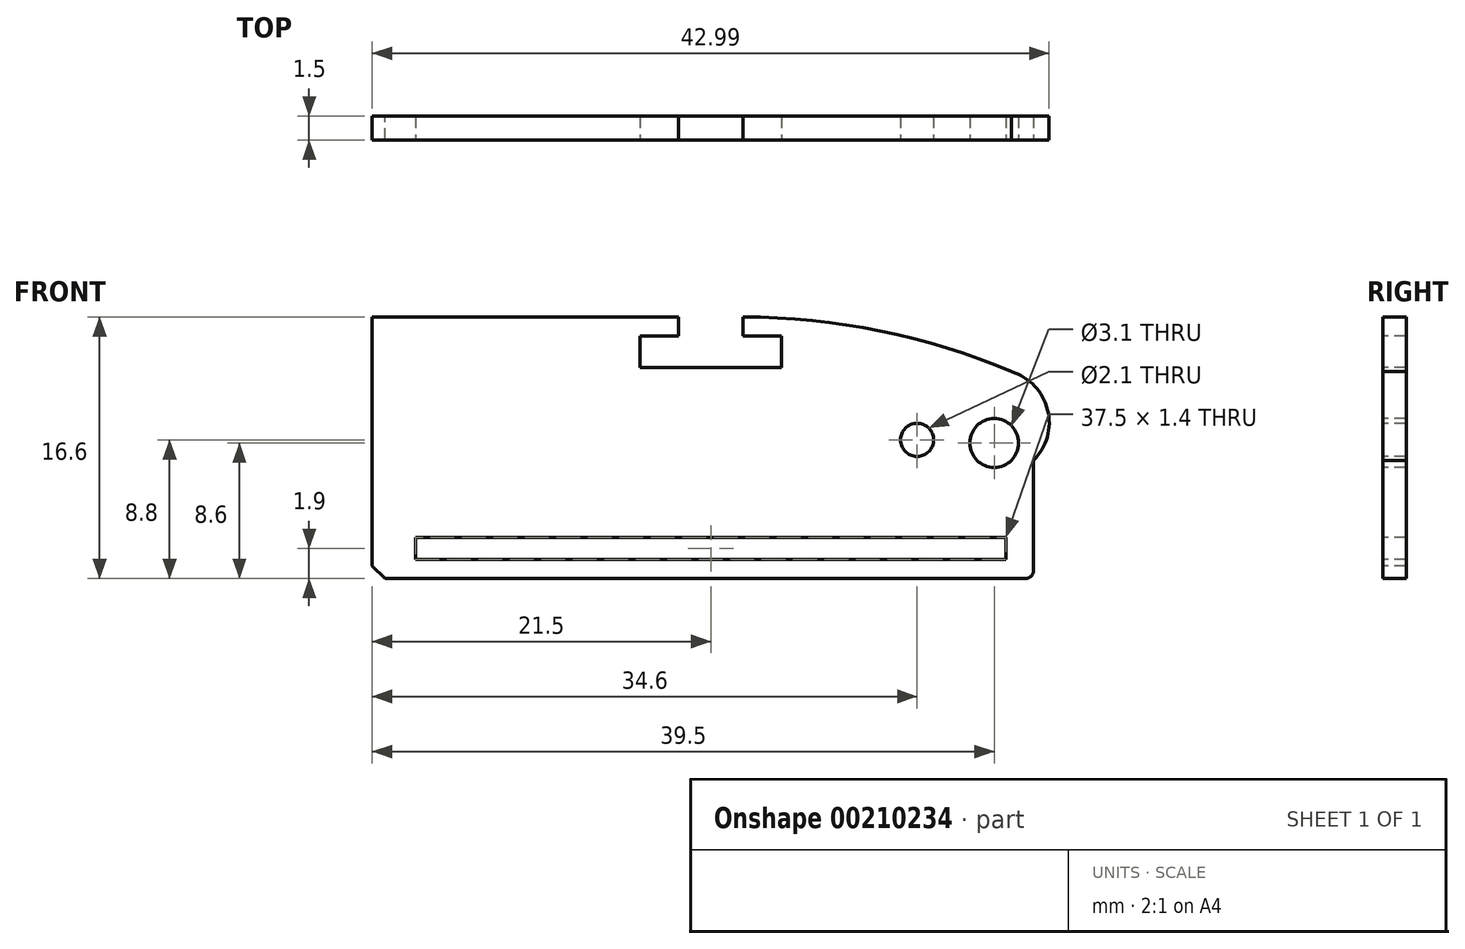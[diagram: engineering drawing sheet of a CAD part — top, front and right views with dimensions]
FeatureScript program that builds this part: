
annotation { "Feature Type Name" : "Feature", "Feature Type Description" : "" }
export const myFeature = defineFeature(function(context is Context, id is Id, definition is map)
    precondition{}
    {
        {
            var Q0;
            Q0=qCreatedBy(makeId("Front.planeOp"),FACE);
            var sketch = newSketch(context, id + "F0", { "sketchPlane" : qUnion([Q0])});
            skLineSegment(sketch, "E0.bottom", {"start": v(-21.5, 8.3) * mm, "end": v(21.5, 8.3) * mm});
            skLineSegment(sketch, "E0.top", {"start": v(-21.5, -8.3) * mm, "end": v(21.5, -8.3) * mm});
            skLineSegment(sketch, "E0.left", {"start": v(-21.5, 8.3) * mm, "end": v(-21.5, -8.3) * mm});
            skLineSegment(sketch, "E0.right", {"start": v(21.5, 8.3) * mm, "end": v(21.5, -8.3) * mm});
            skPoint(sketch, "E0.middle", {"position": v(0, 0) * mm});
            skPoint(sketch, "E1.middle", {"position": v(0, -8.3) * mm});
            skPoint(sketch, "E2.middle", {"position": v(0, -1.7) * mm});
            skSolve(sketch);
        }
        {
            var Q0;
            Q0=makeQuery(id+"F0.imprint","IMPRINT",FACE,{"disambiguationData":[TD([[makeQuery(id+"F0.imprint","IMPRINT",EDGE,{"derivedFrom":sQuery(id+"F0.wireOp",EDGE,"E0.bottom")}),-1.0]])]});
            extrude(context, id + "F1", {"entities" : qUnion([Q0]), "endBound" : BoundingType.SYMMETRIC, "depth" : 1.5 * mm});
        }
        {
            var Q0;
            Q0=qCreatedBy(makeId("Front.planeOp"),FACE);
            var sketch = newSketch(context, id + "F2", { "sketchPlane" : qUnion([Q0])});
            skLineSegment(sketch, "E3.bottom", {"start": v(-18.75, -5.7) * mm, "end": v(18.75, -5.7) * mm});
            skLineSegment(sketch, "E3.top", {"start": v(-18.75, -7.1) * mm, "end": v(18.75, -7.1) * mm});
            skLineSegment(sketch, "E3.left", {"start": v(-18.75, -5.7) * mm, "end": v(-18.75, -7.1) * mm});
            skLineSegment(sketch, "E3.right", {"start": v(18.75, -5.7) * mm, "end": v(18.75, -7.1) * mm});
            skPoint(sketch, "E3.middle", {"position": v(0, -6.4) * mm});
            skSolve(sketch);
        }
        {
            var Q0;
            Q0=qSketchRegion(id+"F2",true);
            extrude(context, id + "F3", {"entities" : qUnion([Q0]), "operationType" : NewBodyOperationType.REMOVE, "endBound" : BoundingType.SYMMETRIC, "oppositeDirection" : true, "depth" : 150 * mm});
        }
        {
            var Q0;
            Q0=makeQuery(id+"F1.opExtrude","SWEPT_EDGE",EDGE,{"disambiguationData":[OSD([sQuery(id+"F0.wireOp",EDGE,"E0.top"),sQuery(id+"F0.wireOp",EDGE,"E1.left")])]});
            var Q1;
            Q1=makeQuery(id+"F1.opExtrude","SWEPT_EDGE",EDGE,{"disambiguationData":[OSD([sQuery(id+"F0.wireOp",EDGE,"E0.top"),sQuery(id+"F0.wireOp",EDGE,"E1.right")])]});
            chamfer(context, id + "F4", {"entities" : qUnion([Q0, Q1]), "width" : .8 * mm, "tangentPropagation" : true});
        }
        {
            var Q0;
            Q0=makeQuery(id+"F1.opExtrude","CAP_FACE",FACE,{"disambiguationData":[OSD([sQuery(id+"F0.wireOp",EDGE,"E0.bottom"),sQuery(id+"F0.wireOp",EDGE,"E0.top"),sQuery(id+"F0.wireOp",EDGE,"E0.left"),sQuery(id+"F0.wireOp",EDGE,"E0.right"),sQuery(id+"F0.wireOp",EDGE,"E1.bottom"),sQuery(id+"F0.wireOp",EDGE,"E1.left"),sQuery(id+"F0.wireOp",EDGE,"E1.right"),sQuery(id+"F0.wireOp",EDGE,"E2.bottom"),sQuery(id+"F0.wireOp",EDGE,"E2.left"),sQuery(id+"F0.wireOp",EDGE,"E2.right")])],"isStart":false});
            var sketch = newSketch(context, id + "F5", { "sketchPlane" : qUnion([Q0])});
            skCircle(sketch, "E4", {"center": v(13.1, 0.5) * mm, "radius": 1.05 * mm});
            skCircle(sketch, "E5", {"center": v(18, 0.3) * mm, "radius": 1.55 * mm});
            skPoint(sketch, "E6.middle", {"position": v(13.1, -1.7) * mm});
            skSolve(sketch);
        }
        {
            var Q0;
            Q0=qSketchRegion(id+"F5",true);
            extrude(context, id + "F6", {"entities" : qUnion([Q0]), "operationType" : NewBodyOperationType.REMOVE, "endBound" : BoundingType.THROUGH_ALL, "oppositeDirection" : true, "depth" : 25 * mm});
        }
        {
            var Q0;
            Q0=makeQuery(id+"F1.opExtrude","CAP_FACE",FACE,{"disambiguationData":[OSD([sQuery(id+"F0.wireOp",EDGE,"E0.bottom"),sQuery(id+"F0.wireOp",EDGE,"E0.top"),sQuery(id+"F0.wireOp",EDGE,"E0.left"),sQuery(id+"F0.wireOp",EDGE,"E0.right"),sQuery(id+"F0.wireOp",EDGE,"E1.bottom"),sQuery(id+"F0.wireOp",EDGE,"E1.left"),sQuery(id+"F0.wireOp",EDGE,"E1.right"),sQuery(id+"F0.wireOp",EDGE,"E2.bottom"),sQuery(id+"F0.wireOp",EDGE,"E2.left"),sQuery(id+"F0.wireOp",EDGE,"E2.right")])],"isStart":false});
            var sketch = newSketch(context, id + "F7", { "sketchPlane" : qUnion([Q0])});
            skLineSegment(sketch, "E7.bottom", {"start": v(-4.5, 7.1) * mm, "end": v(4.5, 7.1) * mm});
            skLineSegment(sketch, "E7.top", {"start": v(-4.5, 5.1) * mm, "end": v(4.5, 5.1) * mm});
            skLineSegment(sketch, "E7.left", {"start": v(-4.5, 7.1) * mm, "end": v(-4.5, 5.1) * mm});
            skLineSegment(sketch, "E7.right", {"start": v(4.5, 7.1) * mm, "end": v(4.5, 5.1) * mm});
            skPoint(sketch, "E7.middle", {"position": v(0, 6.1) * mm});
            skLineSegment(sketch, "E8.bottom", {"start": v(-2.05, 9.05) * mm, "end": v(2.05, 9.05) * mm});
            skLineSegment(sketch, "E8.top", {"start": v(-2.05, 6.3) * mm, "end": v(2.05, 6.3) * mm});
            skLineSegment(sketch, "E8.left", {"start": v(-2.05, 9.05) * mm, "end": v(-2.05, 6.3) * mm});
            skLineSegment(sketch, "E8.right", {"start": v(2.05, 9.05) * mm, "end": v(2.05, 6.3) * mm});
            skPoint(sketch, "E8.middle", {"position": v(0, 7.67) * mm});
            skPoint(sketch, "E8.middle.positionSnap0", {"position": v(0, 8.3) * mm});
            skPoint(sketch, "E8.centerSnap0", {"position": v(0, 8.3) * mm});
            skLineSegment(sketch, "E9.bottom", {"start": v(20.5, -0.8) * mm, "end": v(22.5, -0.8) * mm});
            skLineSegment(sketch, "E9.top", {"start": v(20.5, -15.8) * mm, "end": v(22.5, -15.8) * mm});
            skLineSegment(sketch, "E9.left", {"start": v(20.5, -0.8) * mm, "end": v(20.5, -15.8) * mm});
            skLineSegment(sketch, "E9.right", {"start": v(22.5, -0.8) * mm, "end": v(22.5, -15.8) * mm});
            skPoint(sketch, "E9.middle", {"position": v(21.5, -8.3) * mm});
            skSolve(sketch);
        }
        {
            var Q0;
            Q0=qSketchRegion(id+"F7",true);
            extrude(context, id + "F8", {"entities" : qUnion([Q0]), "operationType" : NewBodyOperationType.REMOVE, "endBound" : BoundingType.THROUGH_ALL, "oppositeDirection" : true, "depth" : 150 * mm});
        }
        {
            var Q0;
            Q0=makeQuery(id+"F1.opExtrude","CAP_FACE",FACE,{"disambiguationData":[OSD([sQuery(id+"F0.wireOp",EDGE,"E0.bottom"),sQuery(id+"F0.wireOp",EDGE,"E0.top"),sQuery(id+"F0.wireOp",EDGE,"E0.left"),sQuery(id+"F0.wireOp",EDGE,"E0.right"),sQuery(id+"F0.wireOp",EDGE,"E1.bottom"),sQuery(id+"F0.wireOp",EDGE,"E1.left"),sQuery(id+"F0.wireOp",EDGE,"E1.right"),sQuery(id+"F0.wireOp",EDGE,"E2.bottom"),sQuery(id+"F0.wireOp",EDGE,"E2.left"),sQuery(id+"F0.wireOp",EDGE,"E2.right")])],"isStart":false});
            var sketch = newSketch(context, id + "F9", { "sketchPlane" : qUnion([Q0])});
            skArc(sketch, "E10", {"start": v(19.1, 4.83) * mm, "mid": v(10.75, 7.42) * mm, "end": v(2.05, 8.3) * mm});
            skArc(sketch, "E11", {"start": v(20.5, -0.8) * mm, "mid": v(21.4, 2.4) * mm, "end": v(19.1, 4.83) * mm});
            skLineSegment(sketch, "E12", {"start": v(2.05, 8.3) * mm, "end": v(22.57, 15.81) * mm});
            skLineSegment(sketch, "E13", {"start": v(22.57, 15.81) * mm, "end": v(29.88, -7.1) * mm});
            skLineSegment(sketch, "E14", {"start": v(29.88, -7.1) * mm, "end": v(20.5, -0.8) * mm});
            skSolve(sketch);
        }
        {
            var Q0;
            Q0=qSketchRegion(id+"F9",true);
            extrude(context, id + "F10", {"entities" : qUnion([Q0]), "operationType" : NewBodyOperationType.REMOVE, "endBound" : BoundingType.THROUGH_ALL, "oppositeDirection" : true, "depth" : 25 * mm});
        }
        {
            var Q0;
            Q0=makeQuery(id+"F74LCkU0cAwYPBq_1.boolean.opBoolean","INTERSECT",EDGE,{"derivedFrom":[makeQuery(id+"F7Wg1tdsILvHaEP_1.boolean.opBoolean","SPLIT",FACE,{"disambiguationData":[TD([makeQuery(id+"F10.boolean.opBoolean","COPY",FACE,{"derivedFrom":makeQuery(id+"F10.opExtrude","SWEPT_FACE",FACE,{"disambiguationData":[OSD([sQuery(id+"F9.wireOp",EDGE,"E11")])]})})])],"derivedFrom":makeQuery(id+"F10.boolean.opBoolean","COPY",FACE,{"derivedFrom":makeQuery(id+"F10.opExtrude","SWEPT_FACE",FACE,{"disambiguationData":[OSD([sQuery(id+"F9.wireOp",EDGE,"E10")])]})})}),makeQuery(id+"F74LCkU0cAwYPBq_1.opExtrude","SWEPT_FACE",FACE,{"disambiguationData":[OSD([sQuery(id+"Fj5Cu2meqdxAn1M_1.wireOp",EDGE,"a9036be3-589b-456a-b4ab-10f7ee7461ad.1.0.1")])]})]});
            var Q1;
            Q1=makeQuery(id+"F74LCkU0cAwYPBq_1.boolean.opBoolean","INTERSECT",EDGE,{"derivedFrom":[makeQuery(id+"F7Wg1tdsILvHaEP_1.boolean.opBoolean","SPLIT",FACE,{"disambiguationData":[TD([makeQuery(id+"F10.boolean.opBoolean","COPY",FACE,{"derivedFrom":makeQuery(id+"F10.opExtrude","SWEPT_FACE",FACE,{"disambiguationData":[OSD([sQuery(id+"F9.wireOp",EDGE,"E11")])]})})])],"derivedFrom":makeQuery(id+"F10.boolean.opBoolean","COPY",FACE,{"derivedFrom":makeQuery(id+"F10.opExtrude","SWEPT_FACE",FACE,{"disambiguationData":[OSD([sQuery(id+"F9.wireOp",EDGE,"E10")])]})})}),makeQuery(id+"F74LCkU0cAwYPBq_1.opExtrude","SWEPT_FACE",FACE,{"disambiguationData":[OSD([sQuery(id+"Fj5Cu2meqdxAn1M_1.wireOp",EDGE,"a9036be3-589b-456a-b4ab-10f7ee7461ad.1.0.0")])]})]});
            var Q2;
            Q2=makeQuery(id+"F74LCkU0cAwYPBq_1.boolean.opBoolean","INTERSECT",EDGE,{"derivedFrom":[makeQuery(id+"F7Wg1tdsILvHaEP_1.boolean.opBoolean","SPLIT",FACE,{"disambiguationData":[TD([makeQuery(id+"F10.boolean.opBoolean","COPY",FACE,{"derivedFrom":makeQuery(id+"F10.opExtrude","SWEPT_FACE",FACE,{"disambiguationData":[OSD([sQuery(id+"F9.wireOp",EDGE,"E11")])]})})])],"derivedFrom":makeQuery(id+"F10.boolean.opBoolean","COPY",FACE,{"derivedFrom":makeQuery(id+"F10.opExtrude","SWEPT_FACE",FACE,{"disambiguationData":[OSD([sQuery(id+"F9.wireOp",EDGE,"E10")])]})})}),makeQuery(id+"F74LCkU0cAwYPBq_1.opExtrude","SWEPT_FACE",FACE,{"disambiguationData":[OSD([sQuery(id+"Fj5Cu2meqdxAn1M_1.wireOp",EDGE,"z4xWm9TB-ZNJp-fwBn-XwMe-NYbhaNwm7cxF.right")])]})]});
            var Q3;
            Q3=makeQuery(id+"F74LCkU0cAwYPBq_1.boolean.opBoolean","INTERSECT",EDGE,{"derivedFrom":[makeQuery(id+"F7Wg1tdsILvHaEP_1.boolean.opBoolean","SPLIT",FACE,{"disambiguationData":[TD([makeQuery(id+"F10.boolean.opBoolean","COPY",FACE,{"derivedFrom":makeQuery(id+"F10.opExtrude","SWEPT_FACE",FACE,{"disambiguationData":[OSD([sQuery(id+"F9.wireOp",EDGE,"E11")])]})})])],"derivedFrom":makeQuery(id+"F10.boolean.opBoolean","COPY",FACE,{"derivedFrom":makeQuery(id+"F10.opExtrude","SWEPT_FACE",FACE,{"disambiguationData":[OSD([sQuery(id+"F9.wireOp",EDGE,"E10")])]})})}),makeQuery(id+"F74LCkU0cAwYPBq_1.opExtrude","SWEPT_FACE",FACE,{"disambiguationData":[OSD([sQuery(id+"Fj5Cu2meqdxAn1M_1.wireOp",EDGE,"z4xWm9TB-ZNJp-fwBn-XwMe-NYbhaNwm7cxF.left")])]})]});
            var Q4;
            Q4=makeQuery(id+"F7Wg1tdsILvHaEP_1.boolean.opBoolean","INTERSECT",EDGE,{"derivedFrom":[makeQuery(id+"F10.boolean.opBoolean","COPY",FACE,{"derivedFrom":makeQuery(id+"F10.opExtrude","SWEPT_FACE",FACE,{"disambiguationData":[OSD([sQuery(id+"F9.wireOp",EDGE,"E10")])]})}),makeQuery(id+"F7Wg1tdsILvHaEP_1.opExtrude","SWEPT_FACE",FACE,{"disambiguationData":[OSD([sQuery(id+"FbxsNwfIe2iOzpL_1.wireOp",EDGE,"60cd6b26-d30f-4a72-b625-cd27377d1117.1.0.0")])]})]});
            var Q5;
            Q5=makeQuery(id+"F7Wg1tdsILvHaEP_1.boolean.opBoolean","INTERSECT",EDGE,{"derivedFrom":[makeQuery(id+"F10.boolean.opBoolean","COPY",FACE,{"derivedFrom":makeQuery(id+"F10.opExtrude","SWEPT_FACE",FACE,{"disambiguationData":[OSD([sQuery(id+"F9.wireOp",EDGE,"E10")])]})}),makeQuery(id+"F7Wg1tdsILvHaEP_1.opExtrude","SWEPT_FACE",FACE,{"disambiguationData":[OSD([sQuery(id+"FbxsNwfIe2iOzpL_1.wireOp",EDGE,"60cd6b26-d30f-4a72-b625-cd27377d1117.1.0.1")])]})]});
            var Q6;
            Q6=makeQuery(id+"F7Wg1tdsILvHaEP_1.boolean.opBoolean","INTERSECT",EDGE,{"derivedFrom":[makeQuery(id+"F10.boolean.opBoolean","COPY",FACE,{"derivedFrom":makeQuery(id+"F10.opExtrude","SWEPT_FACE",FACE,{"disambiguationData":[OSD([sQuery(id+"F9.wireOp",EDGE,"E10")])]})}),makeQuery(id+"F7Wg1tdsILvHaEP_1.opExtrude","SWEPT_FACE",FACE,{"disambiguationData":[OSD([sQuery(id+"FbxsNwfIe2iOzpL_1.wireOp",EDGE,"DTDODECN-btGo-K57W-ewbY-CqeMjswKm1TL.right")])]})]});
            var Q7;
            Q7=makeQuery(id+"F7Wg1tdsILvHaEP_1.boolean.opBoolean","INTERSECT",EDGE,{"derivedFrom":[makeQuery(id+"F10.boolean.opBoolean","COPY",FACE,{"derivedFrom":makeQuery(id+"F10.opExtrude","SWEPT_FACE",FACE,{"disambiguationData":[OSD([sQuery(id+"F9.wireOp",EDGE,"E10")])]})}),makeQuery(id+"F7Wg1tdsILvHaEP_1.opExtrude","SWEPT_FACE",FACE,{"disambiguationData":[OSD([sQuery(id+"FbxsNwfIe2iOzpL_1.wireOp",EDGE,"DTDODECN-btGo-K57W-ewbY-CqeMjswKm1TL.left")])]})]});
            var Q8;
            Q8=makeQuery(id+"FLAS50ZotFcGA18_1.1.F7Wg1tdsILvHaEP_1.boolean.opBoolean","INTERSECT",EDGE,{"derivedFrom":[makeQuery(id+"FLAS50ZotFcGA18_1.1.F10.boolean.opBoolean","COPY",FACE,{"derivedFrom":makeQuery(id+"FLAS50ZotFcGA18_1.1.F10.opExtrude","SWEPT_FACE",FACE,{"disambiguationData":[OSD([sQuery(id+"F9.wireOp",EDGE,"E10")])]})}),makeQuery(id+"FLAS50ZotFcGA18_1.1.F7Wg1tdsILvHaEP_1.opExtrude","SWEPT_FACE",FACE,{"disambiguationData":[OSD([sQuery(id+"FbxsNwfIe2iOzpL_1.wireOp",EDGE,"DTDODECN-btGo-K57W-ewbY-CqeMjswKm1TL.left")])]})]});
            var Q9;
            Q9=makeQuery(id+"FLAS50ZotFcGA18_1.1.F7Wg1tdsILvHaEP_1.boolean.opBoolean","INTERSECT",EDGE,{"derivedFrom":[makeQuery(id+"FLAS50ZotFcGA18_1.1.F10.boolean.opBoolean","COPY",FACE,{"derivedFrom":makeQuery(id+"FLAS50ZotFcGA18_1.1.F10.opExtrude","SWEPT_FACE",FACE,{"disambiguationData":[OSD([sQuery(id+"F9.wireOp",EDGE,"E10")])]})}),makeQuery(id+"FLAS50ZotFcGA18_1.1.F7Wg1tdsILvHaEP_1.opExtrude","SWEPT_FACE",FACE,{"disambiguationData":[OSD([sQuery(id+"FbxsNwfIe2iOzpL_1.wireOp",EDGE,"DTDODECN-btGo-K57W-ewbY-CqeMjswKm1TL.right")])]})]});
            var Q10;
            Q10=makeQuery(id+"FLAS50ZotFcGA18_1.1.F7Wg1tdsILvHaEP_1.boolean.opBoolean","INTERSECT",EDGE,{"derivedFrom":[makeQuery(id+"FLAS50ZotFcGA18_1.1.F10.boolean.opBoolean","COPY",FACE,{"derivedFrom":makeQuery(id+"FLAS50ZotFcGA18_1.1.F10.opExtrude","SWEPT_FACE",FACE,{"disambiguationData":[OSD([sQuery(id+"F9.wireOp",EDGE,"E10")])]})}),makeQuery(id+"FLAS50ZotFcGA18_1.1.F7Wg1tdsILvHaEP_1.opExtrude","SWEPT_FACE",FACE,{"disambiguationData":[OSD([sQuery(id+"FbxsNwfIe2iOzpL_1.wireOp",EDGE,"60cd6b26-d30f-4a72-b625-cd27377d1117.1.0.1")])]})]});
            var Q11;
            Q11=makeQuery(id+"FLAS50ZotFcGA18_1.1.F7Wg1tdsILvHaEP_1.boolean.opBoolean","INTERSECT",EDGE,{"derivedFrom":[makeQuery(id+"FLAS50ZotFcGA18_1.1.F10.boolean.opBoolean","COPY",FACE,{"derivedFrom":makeQuery(id+"FLAS50ZotFcGA18_1.1.F10.opExtrude","SWEPT_FACE",FACE,{"disambiguationData":[OSD([sQuery(id+"F9.wireOp",EDGE,"E10")])]})}),makeQuery(id+"FLAS50ZotFcGA18_1.1.F7Wg1tdsILvHaEP_1.opExtrude","SWEPT_FACE",FACE,{"disambiguationData":[OSD([sQuery(id+"FbxsNwfIe2iOzpL_1.wireOp",EDGE,"60cd6b26-d30f-4a72-b625-cd27377d1117.1.0.0")])]})]});
            var Q12;
            Q12=makeQuery(id+"FLAS50ZotFcGA18_1.1.F74LCkU0cAwYPBq_1.boolean.opBoolean","INTERSECT",EDGE,{"derivedFrom":[makeQuery(id+"FLAS50ZotFcGA18_1.1.F7Wg1tdsILvHaEP_1.boolean.opBoolean","SPLIT",FACE,{"disambiguationData":[TD([makeQuery(id+"FLAS50ZotFcGA18_1.1.F10.boolean.opBoolean","COPY",FACE,{"derivedFrom":makeQuery(id+"FLAS50ZotFcGA18_1.1.F10.opExtrude","SWEPT_FACE",FACE,{"disambiguationData":[OSD([sQuery(id+"F9.wireOp",EDGE,"E11")])]})})])],"derivedFrom":makeQuery(id+"FLAS50ZotFcGA18_1.1.F10.boolean.opBoolean","COPY",FACE,{"derivedFrom":makeQuery(id+"FLAS50ZotFcGA18_1.1.F10.opExtrude","SWEPT_FACE",FACE,{"disambiguationData":[OSD([sQuery(id+"F9.wireOp",EDGE,"E10")])]})})}),makeQuery(id+"FLAS50ZotFcGA18_1.1.F74LCkU0cAwYPBq_1.opExtrude","SWEPT_FACE",FACE,{"disambiguationData":[OSD([sQuery(id+"Fj5Cu2meqdxAn1M_1.wireOp",EDGE,"z4xWm9TB-ZNJp-fwBn-XwMe-NYbhaNwm7cxF.left")])]})]});
            var Q13;
            Q13=makeQuery(id+"FLAS50ZotFcGA18_1.1.F74LCkU0cAwYPBq_1.boolean.opBoolean","INTERSECT",EDGE,{"derivedFrom":[makeQuery(id+"FLAS50ZotFcGA18_1.1.F7Wg1tdsILvHaEP_1.boolean.opBoolean","SPLIT",FACE,{"disambiguationData":[TD([makeQuery(id+"FLAS50ZotFcGA18_1.1.F10.boolean.opBoolean","COPY",FACE,{"derivedFrom":makeQuery(id+"FLAS50ZotFcGA18_1.1.F10.opExtrude","SWEPT_FACE",FACE,{"disambiguationData":[OSD([sQuery(id+"F9.wireOp",EDGE,"E11")])]})})])],"derivedFrom":makeQuery(id+"FLAS50ZotFcGA18_1.1.F10.boolean.opBoolean","COPY",FACE,{"derivedFrom":makeQuery(id+"FLAS50ZotFcGA18_1.1.F10.opExtrude","SWEPT_FACE",FACE,{"disambiguationData":[OSD([sQuery(id+"F9.wireOp",EDGE,"E10")])]})})}),makeQuery(id+"FLAS50ZotFcGA18_1.1.F74LCkU0cAwYPBq_1.opExtrude","SWEPT_FACE",FACE,{"disambiguationData":[OSD([sQuery(id+"Fj5Cu2meqdxAn1M_1.wireOp",EDGE,"z4xWm9TB-ZNJp-fwBn-XwMe-NYbhaNwm7cxF.right")])]})]});
            var Q14;
            Q14=makeQuery(id+"FLAS50ZotFcGA18_1.1.F74LCkU0cAwYPBq_1.boolean.opBoolean","INTERSECT",EDGE,{"derivedFrom":[makeQuery(id+"FLAS50ZotFcGA18_1.1.F7Wg1tdsILvHaEP_1.boolean.opBoolean","SPLIT",FACE,{"disambiguationData":[TD([makeQuery(id+"FLAS50ZotFcGA18_1.1.F10.boolean.opBoolean","COPY",FACE,{"derivedFrom":makeQuery(id+"FLAS50ZotFcGA18_1.1.F10.opExtrude","SWEPT_FACE",FACE,{"disambiguationData":[OSD([sQuery(id+"F9.wireOp",EDGE,"E11")])]})})])],"derivedFrom":makeQuery(id+"FLAS50ZotFcGA18_1.1.F10.boolean.opBoolean","COPY",FACE,{"derivedFrom":makeQuery(id+"FLAS50ZotFcGA18_1.1.F10.opExtrude","SWEPT_FACE",FACE,{"disambiguationData":[OSD([sQuery(id+"F9.wireOp",EDGE,"E10")])]})})}),makeQuery(id+"FLAS50ZotFcGA18_1.1.F74LCkU0cAwYPBq_1.opExtrude","SWEPT_FACE",FACE,{"disambiguationData":[OSD([sQuery(id+"Fj5Cu2meqdxAn1M_1.wireOp",EDGE,"a9036be3-589b-456a-b4ab-10f7ee7461ad.1.0.0")])]})]});
            var Q15;
            Q15=makeQuery(id+"FLAS50ZotFcGA18_1.1.F74LCkU0cAwYPBq_1.boolean.opBoolean","INTERSECT",EDGE,{"derivedFrom":[makeQuery(id+"FLAS50ZotFcGA18_1.1.F7Wg1tdsILvHaEP_1.boolean.opBoolean","SPLIT",FACE,{"disambiguationData":[TD([makeQuery(id+"FLAS50ZotFcGA18_1.1.F10.boolean.opBoolean","COPY",FACE,{"derivedFrom":makeQuery(id+"FLAS50ZotFcGA18_1.1.F10.opExtrude","SWEPT_FACE",FACE,{"disambiguationData":[OSD([sQuery(id+"F9.wireOp",EDGE,"E11")])]})})])],"derivedFrom":makeQuery(id+"FLAS50ZotFcGA18_1.1.F10.boolean.opBoolean","COPY",FACE,{"derivedFrom":makeQuery(id+"FLAS50ZotFcGA18_1.1.F10.opExtrude","SWEPT_FACE",FACE,{"disambiguationData":[OSD([sQuery(id+"F9.wireOp",EDGE,"E10")])]})})}),makeQuery(id+"FLAS50ZotFcGA18_1.1.F74LCkU0cAwYPBq_1.opExtrude","SWEPT_FACE",FACE,{"disambiguationData":[OSD([sQuery(id+"Fj5Cu2meqdxAn1M_1.wireOp",EDGE,"a9036be3-589b-456a-b4ab-10f7ee7461ad.1.0.1")])]})]});
            var Q16;
            {var subQ0=sQuery(id+"F0.wireOp",EDGE,"E0.top");Q16=makeQuery(id+"FXWVg8Q61zknNTf_1.1.F8.boolean.opBoolean","INTERSECT",EDGE,{"derivedFrom":[makeQuery(id+"F1.opExtrude","SWEPT_FACE",FACE,{"disambiguationData":[OSD([subQ0]),TDD([makeQuery(id+"F0.imprint","IMPRINT",EDGE,{"disambiguationData":[TD([[makeQuery(id+"F0.imprint","INTERSECT",VERTEX,{"derivedFrom":[subQ0,sQuery(id+"F0.wireOp",EDGE,"E0.left")]}),-1.0]])],"derivedFrom":subQ0})])]}),makeQuery(id+"FXWVg8Q61zknNTf_1.1.F8.opExtrude","SWEPT_FACE",FACE,{"disambiguationData":[OSD([sQuery(id+"F7.wireOp",EDGE,"E9.left")])]})]});}
            var Q17;
            {var subQ0=sQuery(id+"F0.wireOp",EDGE,"E0.top");Q17=makeQuery(id+"F8.boolean.opBoolean","INTERSECT",EDGE,{"derivedFrom":[makeQuery(id+"F1.opExtrude","SWEPT_FACE",FACE,{"disambiguationData":[OSD([subQ0]),TDD([makeQuery(id+"F0.imprint","IMPRINT",EDGE,{"disambiguationData":[TD([[makeQuery(id+"F0.imprint","INTERSECT",VERTEX,{"derivedFrom":[subQ0,sQuery(id+"F0.wireOp",EDGE,"E0.right")]}),1.0]])],"derivedFrom":subQ0})])]}),makeQuery(id+"F8.opExtrude","SWEPT_FACE",FACE,{"disambiguationData":[OSD([sQuery(id+"F7.wireOp",EDGE,"E9.left")])]})]});}
            fillet(context, id + "F11", {"entities" : qUnion([Q0, Q1, Q2, Q3, Q4, Q5, Q6, Q7, Q8, Q9, Q10, Q11, Q12, Q13, Q14, Q15, Q16, Q17]), "radius" : .5 * mm, "tangentPropagation" : true, "allowEdgeOverflow" : false});
        }
    });
